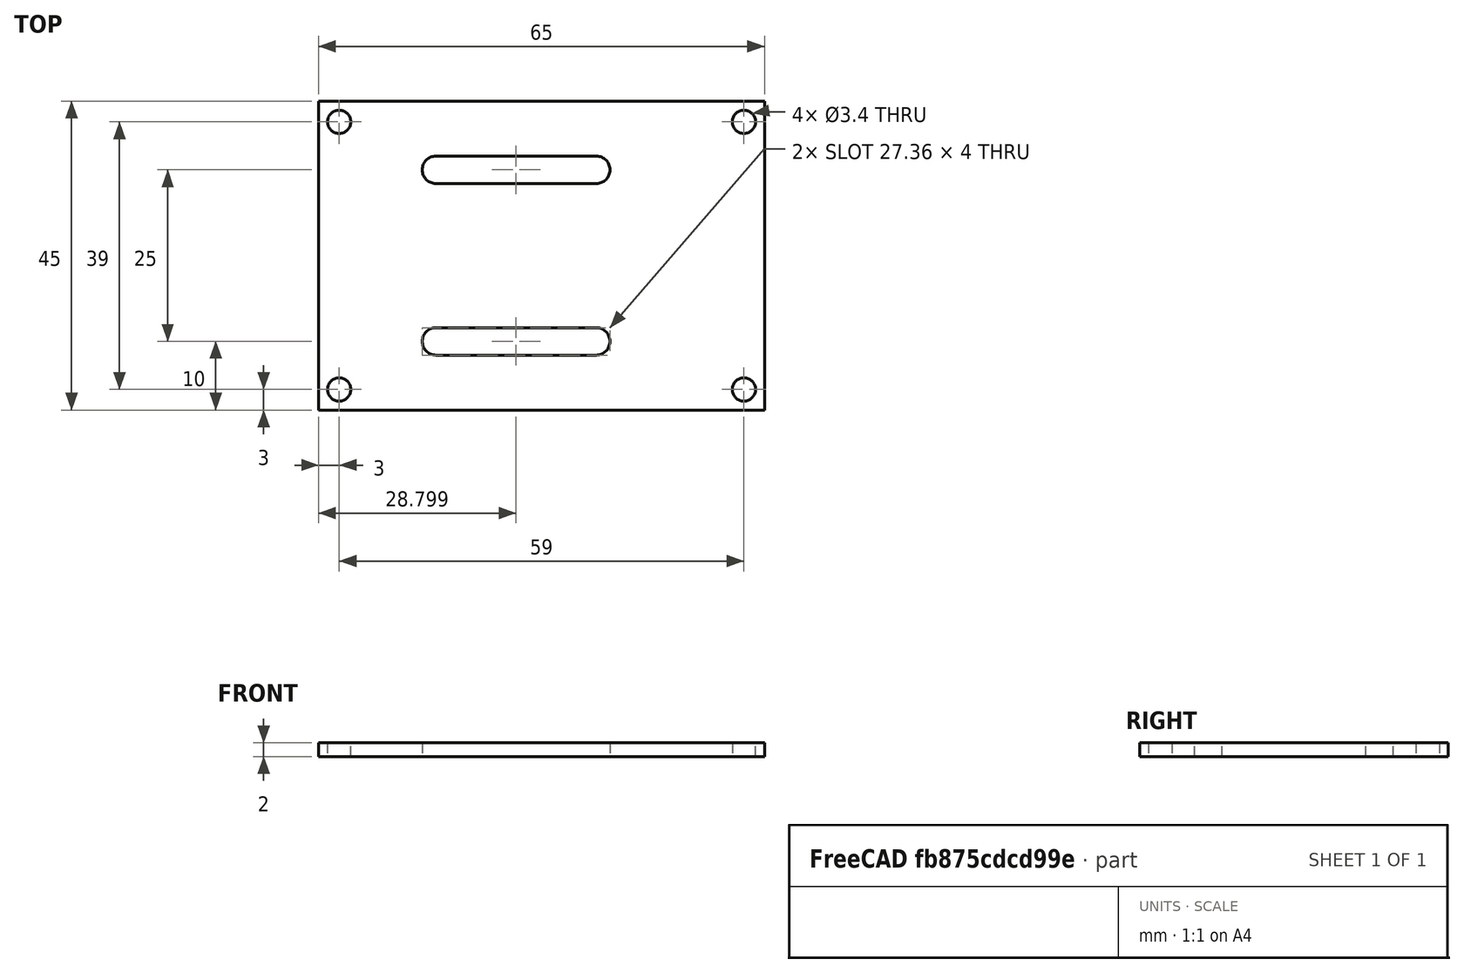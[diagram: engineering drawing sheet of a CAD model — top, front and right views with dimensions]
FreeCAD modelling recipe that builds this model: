
FCSTD DOCUMENT  (FreeCAD 0.17R13515 (Git))
Label: Tampa
License: All rights reserved
LicenseURL: http://en.wikipedia.org/wiki/All_rights_reserved
objects: Sketcher::SketchObject×1, PartDesign::Pad×1, PartDesign::Body×1
note: 4 computed .brp shape members not serialized (recipe doc carries the construction recipe); baked Part::Feature solids carry a one-line shape summary decoded from their .brp

FEATURE [Sketcher::SketchObject] Sketch
  MapMode = 5
  Support = -> [XY_Plane]
  sketch-geometry (21):
    g0: LineSegment StartX=0 StartY=45 StartZ=0 EndX=65 EndY=45 EndZ=0
    g1: LineSegment StartX=65 StartY=45 StartZ=0 EndX=65 EndY=0 EndZ=0
    g2: LineSegment StartX=65 StartY=0 StartZ=0 EndX=0 EndY=0 EndZ=0
    g3: LineSegment StartX=0 StartY=0 StartZ=0 EndX=0 EndY=45 EndZ=0
    g4: LineSegment [constr] StartX=3 StartY=42 StartZ=0 EndX=62 EndY=42 EndZ=0
    g5: LineSegment [constr] StartX=62 StartY=42 StartZ=0 EndX=62 EndY=3 EndZ=0
    g6: LineSegment [constr] StartX=62 StartY=3 StartZ=0 EndX=3 EndY=3 EndZ=0
    g7: LineSegment [constr] StartX=3 StartY=3 StartZ=0 EndX=3 EndY=42 EndZ=0
    g8: Circle CenterX=3 CenterY=42 CenterZ=0 NormalX=0 NormalY=0 NormalZ=1 AngleXU=0 Radius=1.7
    g9: Circle CenterX=62 CenterY=42 CenterZ=0 NormalX=0 NormalY=0 NormalZ=1 AngleXU=0 Radius=1.7
    g10: Circle CenterX=3 CenterY=3 CenterZ=0 NormalX=0 NormalY=0 NormalZ=1 AngleXU=0 Radius=1.7
    g11: Circle CenterX=62 CenterY=3 CenterZ=0 NormalX=0 NormalY=0 NormalZ=1 AngleXU=0 Radius=1.7
    g12: LineSegment [constr] StartX=0 StartY=22.5 StartZ=0 EndX=17.1184 EndY=22.5 EndZ=0
    g13: ArcOfCircle CenterX=17.1184 CenterY=35 CenterZ=0 NormalX=0 NormalY=0 NormalZ=1 AngleXU=0 Radius=2 StartAngle=1.5708 EndAngle=4.71239
    g14: ArcOfCircle CenterX=40.479 CenterY=35 CenterZ=0 NormalX=0 NormalY=0 NormalZ=1 AngleXU=0 Radius=2 StartAngle=4.71239 EndAngle=7.85398
    g15: LineSegment StartX=17.1184 StartY=33 StartZ=0 EndX=40.479 EndY=33 EndZ=0
    g16: LineSegment StartX=17.1184 StartY=37 StartZ=0 EndX=40.479 EndY=37 EndZ=0
    g17: ArcOfCircle CenterX=17.1184 CenterY=10 CenterZ=0 NormalX=0 NormalY=0 NormalZ=1 AngleXU=0 Radius=2 StartAngle=1.5708 EndAngle=4.71239
    g18: ArcOfCircle CenterX=40.479 CenterY=10 CenterZ=0 NormalX=0 NormalY=0 NormalZ=1 AngleXU=0 Radius=2 StartAngle=4.71239 EndAngle=7.85398
    g19: LineSegment StartX=17.1184 StartY=8 StartZ=0 EndX=40.479 EndY=8 EndZ=0
    g20: LineSegment StartX=17.1184 StartY=12 StartZ=0 EndX=40.479 EndY=12 EndZ=0
  constraints (51):
    c: Coincident(g0,g1)
    c: Coincident(g1,g2)
    c: Coincident(g2,g3)
    c: Coincident(g3,g0)
    c: Horizontal(g0)
    c: Horizontal(g2)
    c: Vertical(g1)
    c: Vertical(g3)
    c: Coincident(g2,g-1)
    c: DistanceY(g3,g3) = 45
    c: DistanceX(g0,g0) = 65
    c: Coincident(g4,g5)
    c: Coincident(g5,g6)
    c: Coincident(g6,g7)
    c: Coincident(g7,g4)
    c: Horizontal(g4)
    c: Horizontal(g6)
    c: Vertical(g5)
    c: Vertical(g7)
    c: DistanceX(g5,g1) = 3
    c: DistanceY(g1,g5) = 3
    c: DistanceX(g0,g4) = 3
    c: DistanceY(g4,g0) = 3
    c: Radius(g8) = 1.7
    c: Equal(g8,g9)
    c: Equal(g8,g10)
    c: Equal(g8,g11)
    c: Coincident(g4,g8)
    c: Coincident(g4,g9)
    c: Coincident(g11,g5)
    c: Coincident(g6,g10)
    c: Horizontal(g12)
    c: Symmetric(g0,g-1,g12)
    c: Tangent(g13,g16) = 1.5708
    c: Tangent(g13,g15) = -1.5708
    c: Tangent(g15,g14) = -1.5708
    c: Tangent(g16,g14) = 1.5708
    c: Horizontal(g15)
    c: Equal(g13,g14)
    c: Tangent(g17,g20) = 1.5708
    c: Tangent(g17,g19) = -1.5708
    c: Tangent(g19,g18) = -1.5708
    c: Tangent(g20,g18) = 1.5708
    c: Horizontal(g19)
    c: Equal(g17,g18)
    c: DistanceY(g17,g13) = 29
    c: DistanceY(g14,g14) = 4
    c: DistanceY(g18,g18) = 4
    c: Equal(g16,g20)
    c: Symmetric(g13,g17,g12)
    c: DistanceX(g17,g12) = 0
FEATURE [PartDesign::Pad] Pad
  Length = 2
  Length2 = 100
  Profile = -> Sketch
  Type = 0
FEATURE [PartDesign::Body] Body
  Group = -> [Sketch,Pad]
  Origin = -> Origin
  Tip = -> Pad
